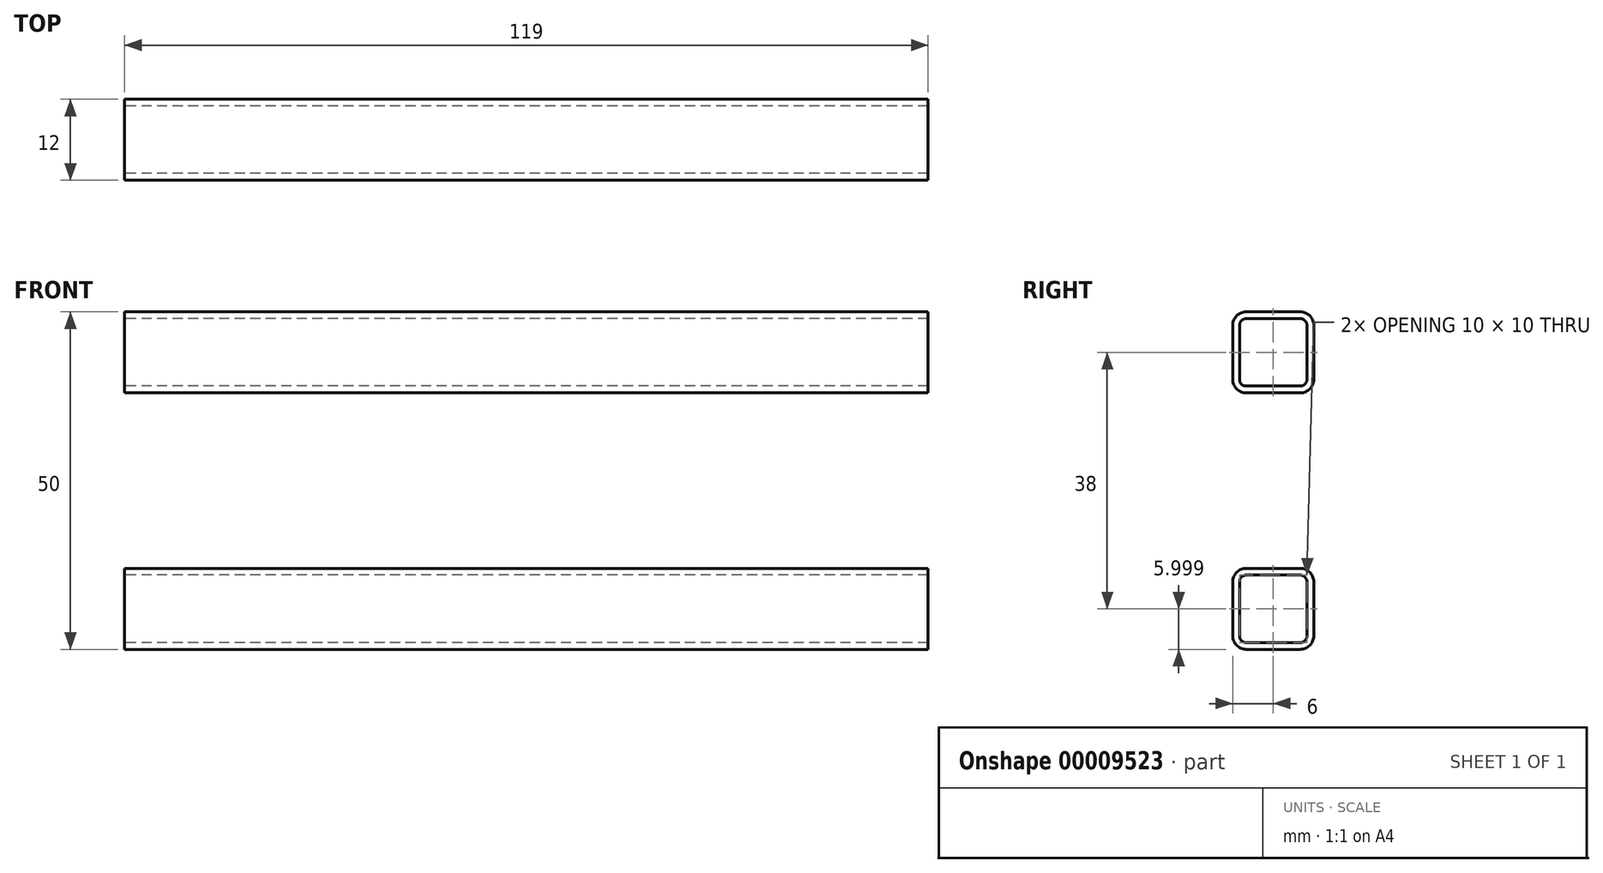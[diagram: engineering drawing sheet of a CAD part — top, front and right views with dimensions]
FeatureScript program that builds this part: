
annotation { "Feature Type Name" : "Feature", "Feature Type Description" : "" }
export const myFeature = defineFeature(function(context is Context, id is Id, definition is map)
    precondition{}
    {
        {
            var Q0;
            Q0=qCreatedBy(makeId("Front.planeOp"),FACE);
            var sketch = newSketch(context, id + "F0", { "sketchPlane" : qUnion([Q0])});
            skLineSegment(sketch, "E0", {"start": v(-60.2, 31.39) * mm, "end": v(58.8, 31.39) * mm});
            skLineSegment(sketch, "E1", {"start": v(-56.2, 36.39) * mm, "end": v(-56.2, -28.61) * mm});
            skLineSegment(sketch, "E2", {"start": v(53.8, 36.39) * mm, "end": v(53.8, -23.61) * mm});
            skLineSegment(sketch, "E3", {"start": v(58.8, -18.61) * mm, "end": v(-60.2, -18.61) * mm});
            skSolve(sketch);
        }
        {
            var Q0;
            Q0=sQuery(id+"F0.wireOp",VERTEX,"E1.end");
            var Q1;
            Q1=sQuery(id+"F0.wireOp",EDGE,"E1");
            cPlane(context, id + "F1", {"entities" : qUnion([Q0, Q1]), "cplaneType" : CPlaneType.LINE_POINT, "offset" : 150 * mm, "width" : 150 * mm, "height" : 150 * mm});
        }
        {
            var Q0;
            Q0=sQuery(id+"F0.wireOp",VERTEX,"E1.start");
            var Q1;
            Q1=sQuery(id+"F0.wireOp",EDGE,"E1");
            cPlane(context, id + "F2", {"entities" : qUnion([Q0, Q1]), "cplaneType" : CPlaneType.LINE_POINT, "offset" : 150 * mm, "width" : 150 * mm, "height" : 150 * mm});
        }
        {
            var Q0;
            Q0=qCreatedBy(id+"F1.planeOp",FACE);
            var sketch = newSketch(context, id + "F3", { "sketchPlane" : qUnion([Q0])});
            skLineSegment(sketch, "E4.bottom", {"start": v(-54.2, -12.5) * mm, "end": v(-46.2, -12.5) * mm});
            skLineSegment(sketch, "E4.top", {"start": v(-54.2, 12.5) * mm, "end": v(-46.2, 12.5) * mm});
            skLineSegment(sketch, "E4.left", {"start": v(-56.2, -10.5) * mm, "end": v(-56.2, 10.5) * mm});
            skLineSegment(sketch, "E4.right", {"start": v(-44.2, -10.5) * mm, "end": v(-44.2, 10.5) * mm});
            skPoint(sketch, "E5.visualSharp", {"position": v(-56.2, 12.5) * mm});
            skArc(sketch, "E5.filletArc", {"start": v(-54.2, 12.5) * mm, "mid": v(-55.62, 11.91) * mm, "end": v(-56.2, 10.5) * mm});
            skPoint(sketch, "E6.visualSharp", {"position": v(-44.2, 12.5) * mm});
            skArc(sketch, "E6.filletArc", {"start": v(-44.2, 10.5) * mm, "mid": v(-44.8, 11.91) * mm, "end": v(-46.2, 12.5) * mm});
            skPoint(sketch, "E7.visualSharp", {"position": v(-44.2, -12.5) * mm});
            skArc(sketch, "E7.filletArc", {"start": v(-46.2, -12.5) * mm, "mid": v(-44.8, -11.91) * mm, "end": v(-44.2, -10.5) * mm});
            skPoint(sketch, "E8.visualSharp", {"position": v(-56.2, -12.5) * mm});
            skArc(sketch, "E8.filletArc", {"start": v(-56.2, -10.5) * mm, "mid": v(-55.62, -11.91) * mm, "end": v(-54.2, -12.5) * mm});
            skArc(sketch, "E9.0", {"start": v(-54.2, 11.5) * mm, "mid": v(-54.91, 11.2) * mm, "end": v(-55.2, 10.5) * mm});
            skLineSegment(sketch, "E9.1", {"start": v(-55.2, -10.5) * mm, "end": v(-55.2, 10.5) * mm});
            skArc(sketch, "E9.2", {"start": v(-55.2, -10.5) * mm, "mid": v(-54.91, -11.2) * mm, "end": v(-54.2, -11.5) * mm});
            skLineSegment(sketch, "E9.3", {"start": v(-54.2, -11.5) * mm, "end": v(-46.2, -11.5) * mm});
            skArc(sketch, "E9.4", {"start": v(-46.2, -11.5) * mm, "mid": v(-45.5, -11.2) * mm, "end": v(-45.2, -10.5) * mm});
            skLineSegment(sketch, "E9.5", {"start": v(-54.2, 11.5) * mm, "end": v(-46.2, 11.5) * mm});
            skLineSegment(sketch, "E9.6", {"start": v(-45.2, -10.5) * mm, "end": v(-45.2, 10.5) * mm});
            skArc(sketch, "E9.7", {"start": v(-45.2, 10.5) * mm, "mid": v(-45.5, 11.2) * mm, "end": v(-46.2, 11.5) * mm});
            skSolve(sketch);
        }
        {
            var Q0;
            Q0 = qSketchRegion(id + "F3", true);
            var Q1;
            Q1=qCreatedBy(id+"F2.planeOp",FACE);
            extrude(context, id + "F4", {"entities" : qUnion([Q0]), "endBound" : BoundingType.UP_TO_SURFACE, "oppositeDirection" : true, "endBoundEntityFace" : qUnion([Q1]), "depth" : 25 * mm});
        }
        {
            var Q0;
            Q0=sQuery(id+"F0.wireOp",EDGE,"E2");
            var Q1;
            Q1=sQuery(id+"F0.wireOp",VERTEX,"E2.end");
            cPlane(context, id + "F5", {"entities" : qUnion([Q0, Q1]), "cplaneType" : CPlaneType.LINE_POINT, "offset" : 150 * mm, "width" : 150 * mm, "height" : 150 * mm});
        }
        {
            var Q0;
            Q0=qCreatedBy(id+"F5.planeOp",FACE);
            var sketch = newSketch(context, id + "F6", { "sketchPlane" : qUnion([Q0])});
            skLineSegment(sketch, "E10.bottom", {"start": v(43.8, -12.5) * mm, "end": v(51.8, -12.5) * mm});
            skLineSegment(sketch, "E10.top", {"start": v(43.8, 12.5) * mm, "end": v(51.8, 12.5) * mm});
            skLineSegment(sketch, "E10.left", {"start": v(41.8, -10.5) * mm, "end": v(41.8, 10.5) * mm});
            skLineSegment(sketch, "E10.right", {"start": v(53.8, -10.5) * mm, "end": v(53.8, 10.5) * mm});
            skPoint(sketch, "E11.visualSharp", {"position": v(41.8, 12.5) * mm});
            skArc(sketch, "E11.filletArc", {"start": v(43.8, 12.5) * mm, "mid": v(42.38, 11.91) * mm, "end": v(41.8, 10.5) * mm});
            skPoint(sketch, "E12.visualSharp", {"position": v(53.8, 12.5) * mm});
            skArc(sketch, "E12.filletArc", {"start": v(53.8, 10.5) * mm, "mid": v(53.2, 11.91) * mm, "end": v(51.8, 12.5) * mm});
            skPoint(sketch, "E13.visualSharp", {"position": v(53.8, -12.5) * mm});
            skArc(sketch, "E13.filletArc", {"start": v(51.8, -12.5) * mm, "mid": v(53.2, -11.91) * mm, "end": v(53.8, -10.5) * mm});
            skPoint(sketch, "E14.visualSharp", {"position": v(41.8, -12.5) * mm});
            skArc(sketch, "E14.filletArc", {"start": v(41.8, -10.5) * mm, "mid": v(42.38, -11.91) * mm, "end": v(43.8, -12.5) * mm});
            skArc(sketch, "E15.0", {"start": v(43.8, 11.5) * mm, "mid": v(43.09, 11.2) * mm, "end": v(42.8, 10.5) * mm});
            skLineSegment(sketch, "E15.1", {"start": v(42.8, -10.5) * mm, "end": v(42.8, 10.5) * mm});
            skArc(sketch, "E15.2", {"start": v(42.8, -10.5) * mm, "mid": v(43.09, -11.2) * mm, "end": v(43.8, -11.5) * mm});
            skLineSegment(sketch, "E15.3", {"start": v(43.8, -11.5) * mm, "end": v(51.8, -11.5) * mm});
            skArc(sketch, "E15.4", {"start": v(51.8, -11.5) * mm, "mid": v(52.5, -11.2) * mm, "end": v(52.8, -10.5) * mm});
            skLineSegment(sketch, "E15.5", {"start": v(43.8, 11.5) * mm, "end": v(51.8, 11.5) * mm});
            skLineSegment(sketch, "E15.6", {"start": v(52.8, -10.5) * mm, "end": v(52.8, 10.5) * mm});
            skArc(sketch, "E15.7", {"start": v(52.8, 10.5) * mm, "mid": v(52.5, 11.2) * mm, "end": v(51.8, 11.5) * mm});
            skSolve(sketch);
        }
        {
            var Q0;
            Q0 = qSketchRegion(id + "F6", true);
            var Q1;
            Q1=qCreatedBy(id+"F2.planeOp",FACE);
            extrude(context, id + "F7", {"entities" : qUnion([Q0]), "endBound" : BoundingType.UP_TO_SURFACE, "oppositeDirection" : true, "endBoundEntityFace" : qUnion([Q1]), "depth" : 25 * mm});
        }
        {
            var Q0;
            Q0=sQuery(id+"F0.wireOp",VERTEX,"E0.start");
            var Q1;
            Q1=sQuery(id+"F0.wireOp",EDGE,"E0");
            cPlane(context, id + "F8", {"entities" : qUnion([Q0, Q1]), "cplaneType" : CPlaneType.LINE_POINT, "offset" : 150 * mm, "width" : 150 * mm, "height" : 150 * mm});
        }
        {
            var Q0;
            Q0=qCreatedBy(id+"F8.planeOp",FACE);
            var sketch = newSketch(context, id + "F9", { "sketchPlane" : qUnion([Q0])});
            skLineSegment(sketch, "E16.bottom", {"start": v(4, 31.39) * mm, "end": v(-4, 31.39) * mm});
            skLineSegment(sketch, "E16.top", {"start": v(4, 19.39) * mm, "end": v(-4, 19.39) * mm});
            skLineSegment(sketch, "E16.left", {"start": v(6, 29.39) * mm, "end": v(6, 21.39) * mm});
            skLineSegment(sketch, "E16.right", {"start": v(-6, 29.39) * mm, "end": v(-6, 21.39) * mm});
            skPoint(sketch, "E17.visualSharp", {"position": v(6, 31.39) * mm});
            skArc(sketch, "E17.filletArc", {"start": v(6, 29.39) * mm, "mid": v(5.41, 30.8) * mm, "end": v(4, 31.39) * mm});
            skPoint(sketch, "E18.visualSharp", {"position": v(-6, 31.39) * mm});
            skArc(sketch, "E18.filletArc", {"start": v(-4, 31.39) * mm, "mid": v(-5.41, 30.8) * mm, "end": v(-6, 29.39) * mm});
            skPoint(sketch, "E19.visualSharp", {"position": v(-6, 19.39) * mm});
            skArc(sketch, "E19.filletArc", {"start": v(-6, 21.39) * mm, "mid": v(-5.41, 19.98) * mm, "end": v(-4, 19.39) * mm});
            skPoint(sketch, "E20.visualSharp", {"position": v(6, 19.39) * mm});
            skArc(sketch, "E20.filletArc", {"start": v(4, 19.39) * mm, "mid": v(5.41, 19.98) * mm, "end": v(6, 21.39) * mm});
            skArc(sketch, "E21.0", {"start": v(5, 29.39) * mm, "mid": v(4.7, 30.1) * mm, "end": v(4, 30.39) * mm});
            skLineSegment(sketch, "E21.1", {"start": v(5, 29.39) * mm, "end": v(5, 21.39) * mm});
            skArc(sketch, "E21.2", {"start": v(4, 20.39) * mm, "mid": v(4.7, 20.68) * mm, "end": v(5, 21.39) * mm});
            skLineSegment(sketch, "E21.3", {"start": v(4, 20.39) * mm, "end": v(-4, 20.39) * mm});
            skArc(sketch, "E21.4", {"start": v(-5, 21.39) * mm, "mid": v(-4.7, 20.68) * mm, "end": v(-4, 20.39) * mm});
            skLineSegment(sketch, "E21.5", {"start": v(4, 30.39) * mm, "end": v(-4, 30.39) * mm});
            skLineSegment(sketch, "E21.6", {"start": v(-5, 29.39) * mm, "end": v(-5, 21.39) * mm});
            skArc(sketch, "E21.7", {"start": v(-4, 30.39) * mm, "mid": v(-4.7, 30.1) * mm, "end": v(-5, 29.39) * mm});
            skPoint(sketch, "E22", {"position": v(0, 19.39) * mm});
            skSolve(sketch);
        }
        {
            var Q0;
            Q0=sQuery(id+"F0.wireOp",VERTEX,"E0.end");
            var Q1;
            Q1=sQuery(id+"F0.wireOp",EDGE,"E0");
            cPlane(context, id + "F10", {"entities" : qUnion([Q0, Q1]), "cplaneType" : CPlaneType.LINE_POINT, "offset" : 150 * mm, "width" : 150 * mm, "height" : 150 * mm});
        }
        {
            var Q0;
            Q0 = qSketchRegion(id + "F9", true);
            var Q1;
            Q1=qCreatedBy(id+"F10.planeOp",FACE);
            extrude(context, id + "F11", {"entities" : qUnion([Q0]), "endBound" : BoundingType.UP_TO_SURFACE, "endBoundEntityFace" : qUnion([Q1]), "depth" : 25 * mm});
        }
        {
            var Q0;
            Q0=makeQuery(id+"F11.opExtrude","SWEPT_BODY",BODY,{"disambiguationData":[OSD([sQuery(id+"F9.wireOp",EDGE,"E16.bottom"),sQuery(id+"F9.wireOp",EDGE,"E16.top"),sQuery(id+"F9.wireOp",EDGE,"E16.left"),sQuery(id+"F9.wireOp",EDGE,"E16.right"),sQuery(id+"F9.wireOp",EDGE,"E17.filletArc"),sQuery(id+"F9.wireOp",EDGE,"E18.filletArc"),sQuery(id+"F9.wireOp",EDGE,"E19.filletArc"),sQuery(id+"F9.wireOp",EDGE,"E20.filletArc"),sQuery(id+"F9.wireOp",EDGE,"E21.0"),sQuery(id+"F9.wireOp",EDGE,"E21.1"),sQuery(id+"F9.wireOp",EDGE,"E21.2"),sQuery(id+"F9.wireOp",EDGE,"E21.3"),sQuery(id+"F9.wireOp",EDGE,"E21.4"),sQuery(id+"F9.wireOp",EDGE,"E21.5"),sQuery(id+"F9.wireOp",EDGE,"E21.6"),sQuery(id+"F9.wireOp",EDGE,"E21.7")])]});
            var Q1;
            Q1=sQuery(id+"F9.wireOp",VERTEX,"E22");
            var Q2;
            Q2=sQuery(id+"F0.wireOp",VERTEX,"E3.end");
            transform(context, id + "F12", {"entities" : qUnion([Q0]), "transformType" : TransformType.TRANSLATION_ENTITY, "oppositeDirectionEntity" : false, "transformLine" : qUnion([Q1, Q2]), "makeCopy" : true});
        }
        {
            var Q0;
            Q0=makeQuery(id+"F11.opExtrude","SWEPT_BODY",BODY,{"disambiguationData":[OSD([sQuery(id+"F9.wireOp",EDGE,"E16.bottom"),sQuery(id+"F9.wireOp",EDGE,"E16.top"),sQuery(id+"F9.wireOp",EDGE,"E16.left"),sQuery(id+"F9.wireOp",EDGE,"E16.right"),sQuery(id+"F9.wireOp",EDGE,"E17.filletArc"),sQuery(id+"F9.wireOp",EDGE,"E18.filletArc"),sQuery(id+"F9.wireOp",EDGE,"E19.filletArc"),sQuery(id+"F9.wireOp",EDGE,"E20.filletArc"),sQuery(id+"F9.wireOp",EDGE,"E21.0"),sQuery(id+"F9.wireOp",EDGE,"E21.1"),sQuery(id+"F9.wireOp",EDGE,"E21.2"),sQuery(id+"F9.wireOp",EDGE,"E21.3"),sQuery(id+"F9.wireOp",EDGE,"E21.4"),sQuery(id+"F9.wireOp",EDGE,"E21.5"),sQuery(id+"F9.wireOp",EDGE,"E21.6"),sQuery(id+"F9.wireOp",EDGE,"E21.7")])]});
            var Q1;
            Q1=makeQuery(id+"F12.opPattern","COPY",BODY,{"derivedFrom":makeQuery(id+"F11.opExtrude","SWEPT_BODY",BODY,{"disambiguationData":[OSD([sQuery(id+"F9.wireOp",EDGE,"E16.bottom"),sQuery(id+"F9.wireOp",EDGE,"E16.top"),sQuery(id+"F9.wireOp",EDGE,"E16.left"),sQuery(id+"F9.wireOp",EDGE,"E16.right"),sQuery(id+"F9.wireOp",EDGE,"E17.filletArc"),sQuery(id+"F9.wireOp",EDGE,"E18.filletArc"),sQuery(id+"F9.wireOp",EDGE,"E19.filletArc"),sQuery(id+"F9.wireOp",EDGE,"E20.filletArc"),sQuery(id+"F9.wireOp",EDGE,"E21.0"),sQuery(id+"F9.wireOp",EDGE,"E21.1"),sQuery(id+"F9.wireOp",EDGE,"E21.2"),sQuery(id+"F9.wireOp",EDGE,"E21.3"),sQuery(id+"F9.wireOp",EDGE,"E21.4"),sQuery(id+"F9.wireOp",EDGE,"E21.5"),sQuery(id+"F9.wireOp",EDGE,"E21.6"),sQuery(id+"F9.wireOp",EDGE,"E21.7")])]}),"instanceName":"1"});
            var Q2;
            Q2=makeQuery(id+"F4.opExtrude","SWEPT_BODY",BODY,{"disambiguationData":[OSD([sQuery(id+"F3.wireOp",EDGE,"E4.bottom"),sQuery(id+"F3.wireOp",EDGE,"E4.top"),sQuery(id+"F3.wireOp",EDGE,"E4.left"),sQuery(id+"F3.wireOp",EDGE,"E4.right"),sQuery(id+"F3.wireOp",EDGE,"E5.filletArc"),sQuery(id+"F3.wireOp",EDGE,"E6.filletArc"),sQuery(id+"F3.wireOp",EDGE,"E7.filletArc"),sQuery(id+"F3.wireOp",EDGE,"E8.filletArc"),sQuery(id+"F3.wireOp",EDGE,"E9.0"),sQuery(id+"F3.wireOp",EDGE,"E9.1"),sQuery(id+"F3.wireOp",EDGE,"E9.2"),sQuery(id+"F3.wireOp",EDGE,"E9.3"),sQuery(id+"F3.wireOp",EDGE,"E9.4"),sQuery(id+"F3.wireOp",EDGE,"E9.5"),sQuery(id+"F3.wireOp",EDGE,"E9.6"),sQuery(id+"F3.wireOp",EDGE,"E9.7")])]});
            var Q3;
            Q3=makeQuery(id+"F7.opExtrude","SWEPT_BODY",BODY,{"disambiguationData":[OSD([sQuery(id+"F6.wireOp",EDGE,"E10.bottom"),sQuery(id+"F6.wireOp",EDGE,"E10.top"),sQuery(id+"F6.wireOp",EDGE,"E10.left"),sQuery(id+"F6.wireOp",EDGE,"E10.right"),sQuery(id+"F6.wireOp",EDGE,"E11.filletArc"),sQuery(id+"F6.wireOp",EDGE,"E12.filletArc"),sQuery(id+"F6.wireOp",EDGE,"E13.filletArc"),sQuery(id+"F6.wireOp",EDGE,"E14.filletArc"),sQuery(id+"F6.wireOp",EDGE,"E15.0"),sQuery(id+"F6.wireOp",EDGE,"E15.1"),sQuery(id+"F6.wireOp",EDGE,"E15.2"),sQuery(id+"F6.wireOp",EDGE,"E15.3"),sQuery(id+"F6.wireOp",EDGE,"E15.4"),sQuery(id+"F6.wireOp",EDGE,"E15.5"),sQuery(id+"F6.wireOp",EDGE,"E15.6"),sQuery(id+"F6.wireOp",EDGE,"E15.7")])]});
            booleanBodies(context, id + "F13", {"operationType" : BooleanOperationType.SUBTRACTION, "tools" : qUnion([Q0, Q1]), "targets" : qUnion([Q2, Q3]), "offset" : true, "offsetAll" : true, "offsetDistance" : 1 * mm, "keepTools" : true});
        }
        {
            var Q0;
            Q0=makeQuery(id+"F13.tempBoolean.opBoolean","SPLIT",BODY,{"disambiguationData":[OD(2.0)],"derivedFrom":makeQuery(id+"F7.opExtrude","SWEPT_BODY",BODY,{"disambiguationData":[OSD([sQuery(id+"F6.wireOp",EDGE,"E10.bottom"),sQuery(id+"F6.wireOp",EDGE,"E10.top"),sQuery(id+"F6.wireOp",EDGE,"E10.left"),sQuery(id+"F6.wireOp",EDGE,"E10.right"),sQuery(id+"F6.wireOp",EDGE,"E11.filletArc"),sQuery(id+"F6.wireOp",EDGE,"E12.filletArc"),sQuery(id+"F6.wireOp",EDGE,"E13.filletArc"),sQuery(id+"F6.wireOp",EDGE,"E14.filletArc"),sQuery(id+"F6.wireOp",EDGE,"E15.0"),sQuery(id+"F6.wireOp",EDGE,"E15.1"),sQuery(id+"F6.wireOp",EDGE,"E15.2"),sQuery(id+"F6.wireOp",EDGE,"E15.3"),sQuery(id+"F6.wireOp",EDGE,"E15.4"),sQuery(id+"F6.wireOp",EDGE,"E15.5"),sQuery(id+"F6.wireOp",EDGE,"E15.6"),sQuery(id+"F6.wireOp",EDGE,"E15.7")])]})});
            var Q1;
            Q1=makeQuery(id+"F13.tempBoolean.opBoolean","SPLIT",BODY,{"disambiguationData":[OD(1.0)],"derivedFrom":makeQuery(id+"F7.opExtrude","SWEPT_BODY",BODY,{"disambiguationData":[OSD([sQuery(id+"F6.wireOp",EDGE,"E10.bottom"),sQuery(id+"F6.wireOp",EDGE,"E10.top"),sQuery(id+"F6.wireOp",EDGE,"E10.left"),sQuery(id+"F6.wireOp",EDGE,"E10.right"),sQuery(id+"F6.wireOp",EDGE,"E11.filletArc"),sQuery(id+"F6.wireOp",EDGE,"E12.filletArc"),sQuery(id+"F6.wireOp",EDGE,"E13.filletArc"),sQuery(id+"F6.wireOp",EDGE,"E14.filletArc"),sQuery(id+"F6.wireOp",EDGE,"E15.0"),sQuery(id+"F6.wireOp",EDGE,"E15.1"),sQuery(id+"F6.wireOp",EDGE,"E15.2"),sQuery(id+"F6.wireOp",EDGE,"E15.3"),sQuery(id+"F6.wireOp",EDGE,"E15.4"),sQuery(id+"F6.wireOp",EDGE,"E15.5"),sQuery(id+"F6.wireOp",EDGE,"E15.6"),sQuery(id+"F6.wireOp",EDGE,"E15.7")])]})});
            var Q2;
            Q2=makeQuery(id+"F13.tempBoolean.opBoolean","SPLIT",BODY,{"disambiguationData":[OD(4.0)],"derivedFrom":makeQuery(id+"F7.opExtrude","SWEPT_BODY",BODY,{"disambiguationData":[OSD([sQuery(id+"F6.wireOp",EDGE,"E10.bottom"),sQuery(id+"F6.wireOp",EDGE,"E10.top"),sQuery(id+"F6.wireOp",EDGE,"E10.left"),sQuery(id+"F6.wireOp",EDGE,"E10.right"),sQuery(id+"F6.wireOp",EDGE,"E11.filletArc"),sQuery(id+"F6.wireOp",EDGE,"E12.filletArc"),sQuery(id+"F6.wireOp",EDGE,"E13.filletArc"),sQuery(id+"F6.wireOp",EDGE,"E14.filletArc"),sQuery(id+"F6.wireOp",EDGE,"E15.0"),sQuery(id+"F6.wireOp",EDGE,"E15.1"),sQuery(id+"F6.wireOp",EDGE,"E15.2"),sQuery(id+"F6.wireOp",EDGE,"E15.3"),sQuery(id+"F6.wireOp",EDGE,"E15.4"),sQuery(id+"F6.wireOp",EDGE,"E15.5"),sQuery(id+"F6.wireOp",EDGE,"E15.6"),sQuery(id+"F6.wireOp",EDGE,"E15.7")])]})});
            var Q3;
            Q3=makeQuery(id+"F13.tempBoolean.opBoolean","SPLIT",BODY,{"disambiguationData":[OD(3.0)],"derivedFrom":makeQuery(id+"F7.opExtrude","SWEPT_BODY",BODY,{"disambiguationData":[OSD([sQuery(id+"F6.wireOp",EDGE,"E10.bottom"),sQuery(id+"F6.wireOp",EDGE,"E10.top"),sQuery(id+"F6.wireOp",EDGE,"E10.left"),sQuery(id+"F6.wireOp",EDGE,"E10.right"),sQuery(id+"F6.wireOp",EDGE,"E11.filletArc"),sQuery(id+"F6.wireOp",EDGE,"E12.filletArc"),sQuery(id+"F6.wireOp",EDGE,"E13.filletArc"),sQuery(id+"F6.wireOp",EDGE,"E14.filletArc"),sQuery(id+"F6.wireOp",EDGE,"E15.0"),sQuery(id+"F6.wireOp",EDGE,"E15.1"),sQuery(id+"F6.wireOp",EDGE,"E15.2"),sQuery(id+"F6.wireOp",EDGE,"E15.3"),sQuery(id+"F6.wireOp",EDGE,"E15.4"),sQuery(id+"F6.wireOp",EDGE,"E15.5"),sQuery(id+"F6.wireOp",EDGE,"E15.6"),sQuery(id+"F6.wireOp",EDGE,"E15.7")])]})});
            var Q4;
            Q4=makeQuery(id+"F13.tempBoolean.opBoolean","SPLIT",BODY,{"disambiguationData":[OD(1.0)],"derivedFrom":makeQuery(id+"F4.opExtrude","SWEPT_BODY",BODY,{"disambiguationData":[OSD([sQuery(id+"F3.wireOp",EDGE,"E4.bottom"),sQuery(id+"F3.wireOp",EDGE,"E4.top"),sQuery(id+"F3.wireOp",EDGE,"E4.left"),sQuery(id+"F3.wireOp",EDGE,"E4.right"),sQuery(id+"F3.wireOp",EDGE,"E5.filletArc"),sQuery(id+"F3.wireOp",EDGE,"E6.filletArc"),sQuery(id+"F3.wireOp",EDGE,"E7.filletArc"),sQuery(id+"F3.wireOp",EDGE,"E8.filletArc"),sQuery(id+"F3.wireOp",EDGE,"E9.0"),sQuery(id+"F3.wireOp",EDGE,"E9.1"),sQuery(id+"F3.wireOp",EDGE,"E9.2"),sQuery(id+"F3.wireOp",EDGE,"E9.3"),sQuery(id+"F3.wireOp",EDGE,"E9.4"),sQuery(id+"F3.wireOp",EDGE,"E9.5"),sQuery(id+"F3.wireOp",EDGE,"E9.6"),sQuery(id+"F3.wireOp",EDGE,"E9.7")])]})});
            var Q5;
            Q5=makeQuery(id+"F13.tempBoolean.opBoolean","SPLIT",BODY,{"disambiguationData":[OD(2.0)],"derivedFrom":makeQuery(id+"F4.opExtrude","SWEPT_BODY",BODY,{"disambiguationData":[OSD([sQuery(id+"F3.wireOp",EDGE,"E4.bottom"),sQuery(id+"F3.wireOp",EDGE,"E4.top"),sQuery(id+"F3.wireOp",EDGE,"E4.left"),sQuery(id+"F3.wireOp",EDGE,"E4.right"),sQuery(id+"F3.wireOp",EDGE,"E5.filletArc"),sQuery(id+"F3.wireOp",EDGE,"E6.filletArc"),sQuery(id+"F3.wireOp",EDGE,"E7.filletArc"),sQuery(id+"F3.wireOp",EDGE,"E8.filletArc"),sQuery(id+"F3.wireOp",EDGE,"E9.0"),sQuery(id+"F3.wireOp",EDGE,"E9.1"),sQuery(id+"F3.wireOp",EDGE,"E9.2"),sQuery(id+"F3.wireOp",EDGE,"E9.3"),sQuery(id+"F3.wireOp",EDGE,"E9.4"),sQuery(id+"F3.wireOp",EDGE,"E9.5"),sQuery(id+"F3.wireOp",EDGE,"E9.6"),sQuery(id+"F3.wireOp",EDGE,"E9.7")])]})});
            var Q6;
            Q6=makeQuery(id+"F13.tempBoolean.opBoolean","SPLIT",BODY,{"disambiguationData":[OD(4.0)],"derivedFrom":makeQuery(id+"F4.opExtrude","SWEPT_BODY",BODY,{"disambiguationData":[OSD([sQuery(id+"F3.wireOp",EDGE,"E4.bottom"),sQuery(id+"F3.wireOp",EDGE,"E4.top"),sQuery(id+"F3.wireOp",EDGE,"E4.left"),sQuery(id+"F3.wireOp",EDGE,"E4.right"),sQuery(id+"F3.wireOp",EDGE,"E5.filletArc"),sQuery(id+"F3.wireOp",EDGE,"E6.filletArc"),sQuery(id+"F3.wireOp",EDGE,"E7.filletArc"),sQuery(id+"F3.wireOp",EDGE,"E8.filletArc"),sQuery(id+"F3.wireOp",EDGE,"E9.0"),sQuery(id+"F3.wireOp",EDGE,"E9.1"),sQuery(id+"F3.wireOp",EDGE,"E9.2"),sQuery(id+"F3.wireOp",EDGE,"E9.3"),sQuery(id+"F3.wireOp",EDGE,"E9.4"),sQuery(id+"F3.wireOp",EDGE,"E9.5"),sQuery(id+"F3.wireOp",EDGE,"E9.6"),sQuery(id+"F3.wireOp",EDGE,"E9.7")])]})});
            var Q7;
            Q7=makeQuery(id+"F13.tempBoolean.opBoolean","SPLIT",BODY,{"disambiguationData":[OD(3.0)],"derivedFrom":makeQuery(id+"F4.opExtrude","SWEPT_BODY",BODY,{"disambiguationData":[OSD([sQuery(id+"F3.wireOp",EDGE,"E4.bottom"),sQuery(id+"F3.wireOp",EDGE,"E4.top"),sQuery(id+"F3.wireOp",EDGE,"E4.left"),sQuery(id+"F3.wireOp",EDGE,"E4.right"),sQuery(id+"F3.wireOp",EDGE,"E5.filletArc"),sQuery(id+"F3.wireOp",EDGE,"E6.filletArc"),sQuery(id+"F3.wireOp",EDGE,"E7.filletArc"),sQuery(id+"F3.wireOp",EDGE,"E8.filletArc"),sQuery(id+"F3.wireOp",EDGE,"E9.0"),sQuery(id+"F3.wireOp",EDGE,"E9.1"),sQuery(id+"F3.wireOp",EDGE,"E9.2"),sQuery(id+"F3.wireOp",EDGE,"E9.3"),sQuery(id+"F3.wireOp",EDGE,"E9.4"),sQuery(id+"F3.wireOp",EDGE,"E9.5"),sQuery(id+"F3.wireOp",EDGE,"E9.6"),sQuery(id+"F3.wireOp",EDGE,"E9.7")])]})});
            deleteBodies(context, id + "F14", {"entities" : qUnion([Q0, Q1, Q2, Q3, Q4, Q5, Q6, Q7])});
        }
        {
            var Q0;
            {var subQ0=sQuery(id+"F3.wireOp",EDGE,"E4.left");var subQ10=sQuery(id+"F3.wireOp",EDGE,"E5.filletArc");Q0=makeQuery(id+"F13.tempBoolean.opBoolean","SPLIT",FACE,{"disambiguationData":[TD([makeQuery(id+"F4.opExtrude","SWEPT_FACE",FACE,{"disambiguationData":[OSD([subQ10])]})])],"derivedFrom":makeQuery(id+"F4.opExtrude","SWEPT_FACE",FACE,{"disambiguationData":[OSD([subQ0])]})});}
            var sketch = newSketch(context, id + "F15", { "sketchPlane" : qUnion([Q0])});
            skLineSegment(sketch, "E23", {"start": v(0, -5.61) * mm, "end": v(0, -19.61) * mm, "construction": true});
            skPoint(sketch, "E24", {"position": v(0, -12.61) * mm});
            skSolve(sketch);
        }
    });
